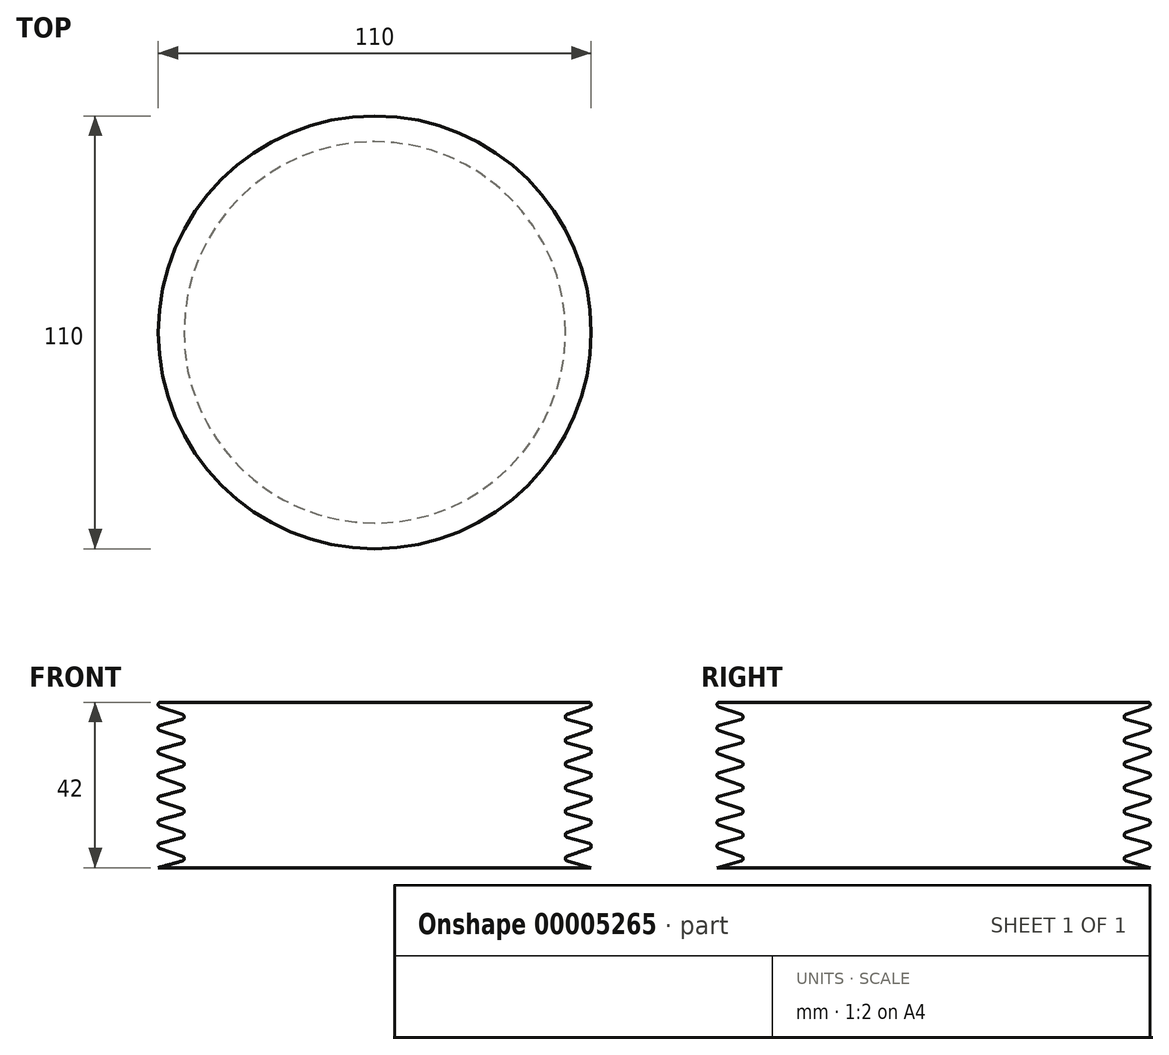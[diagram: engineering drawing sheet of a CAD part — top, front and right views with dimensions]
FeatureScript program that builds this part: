
annotation { "Feature Type Name" : "Feature", "Feature Type Description" : "" }
export const myFeature = defineFeature(function(context is Context, id is Id, definition is map)
    precondition{}
    {
        {
            var Q0;
            Q0=qCreatedBy(makeId("Front.planeOp"),FACE);
            var sketch = newSketch(context, id + "F0", { "sketchPlane" : qUnion([Q0])});
            skLineSegment(sketch, "E0", {"start": v(0, 0) * mm, "end": v(0, 42) * mm});
            skLineSegment(sketch, "E1", {"start": v(-55, 0) * mm, "end": v(-48.46, 1.8) * mm});
            skLineSegment(sketch, "E2", {"start": v(-48.46, 1.8) * mm, "end": v(-48.46, 2.8) * mm});
            skLineSegment(sketch, "E3", {"start": v(-48.46, 2.8) * mm, "end": v(-55, 5) * mm});
            skLineSegment(sketch, "E4", {"start": v(-55, 5) * mm, "end": v(-55, 6) * mm});
            skLineSegment(sketch, "E5.0.1.0", {"start": v(-55, 6) * mm, "end": v(-48.46, 7.8) * mm});
            skLineSegment(sketch, "E5.0.1.1", {"start": v(-48.46, 8.8) * mm, "end": v(-55, 11) * mm});
            skLineSegment(sketch, "E5.0.1.2", {"start": v(-55, 11) * mm, "end": v(-55, 12) * mm});
            skLineSegment(sketch, "E5.0.1.3", {"start": v(-48.46, 7.8) * mm, "end": v(-48.46, 8.8) * mm});
            skLineSegment(sketch, "E5.0.2.0", {"start": v(-55, 12) * mm, "end": v(-48.46, 13.8) * mm});
            skLineSegment(sketch, "E5.0.2.1", {"start": v(-48.46, 14.8) * mm, "end": v(-55, 17) * mm});
            skLineSegment(sketch, "E5.0.2.2", {"start": v(-55, 17) * mm, "end": v(-55, 18) * mm});
            skLineSegment(sketch, "E5.0.2.3", {"start": v(-48.46, 13.8) * mm, "end": v(-48.46, 14.8) * mm});
            skLineSegment(sketch, "E5.0.3.0", {"start": v(-55, 18) * mm, "end": v(-48.46, 19.8) * mm});
            skLineSegment(sketch, "E5.0.3.1", {"start": v(-48.46, 20.8) * mm, "end": v(-55, 23) * mm});
            skLineSegment(sketch, "E5.0.3.2", {"start": v(-55, 23) * mm, "end": v(-55, 24) * mm});
            skLineSegment(sketch, "E5.0.3.3", {"start": v(-48.46, 19.8) * mm, "end": v(-48.46, 20.8) * mm});
            skLineSegment(sketch, "E5.0.4.0", {"start": v(-55, 24) * mm, "end": v(-48.46, 25.8) * mm});
            skLineSegment(sketch, "E5.0.4.1", {"start": v(-48.46, 26.8) * mm, "end": v(-55, 29) * mm});
            skLineSegment(sketch, "E5.0.4.2", {"start": v(-55, 29) * mm, "end": v(-55, 30) * mm});
            skLineSegment(sketch, "E5.0.4.3", {"start": v(-48.46, 25.8) * mm, "end": v(-48.46, 26.8) * mm});
            skLineSegment(sketch, "E5.0.5.0", {"start": v(-55, 30) * mm, "end": v(-48.46, 31.8) * mm});
            skLineSegment(sketch, "E5.0.5.1", {"start": v(-48.46, 32.8) * mm, "end": v(-55, 35) * mm});
            skLineSegment(sketch, "E5.0.5.2", {"start": v(-55, 35) * mm, "end": v(-55, 36) * mm});
            skLineSegment(sketch, "E5.0.5.3", {"start": v(-48.46, 31.8) * mm, "end": v(-48.46, 32.8) * mm});
            skLineSegment(sketch, "E5.0.6.0", {"start": v(-55, 36) * mm, "end": v(-48.46, 37.8) * mm});
            skLineSegment(sketch, "E5.0.6.1", {"start": v(-48.46, 38.8) * mm, "end": v(-55, 41) * mm});
            skLineSegment(sketch, "E5.0.6.2", {"start": v(-55, 41) * mm, "end": v(-55, 42) * mm});
            skLineSegment(sketch, "E5.0.6.3", {"start": v(-48.46, 37.8) * mm, "end": v(-48.46, 38.8) * mm});
            skLineSegment(sketch, "E5.direction1", {"start": v(-55, 0) * mm, "end": v(-14, 0) * mm, "construction": true});
            skLineSegment(sketch, "E5.direction2", {"start": v(-55, 0) * mm, "end": v(-55, 6) * mm, "construction": true});
            skLineSegment(sketch, "E6", {"start": v(-55, 0) * mm, "end": v(0, 0) * mm});
            skLineSegment(sketch, "E7", {"start": v(-55, 42) * mm, "end": v(0, 42) * mm});
            skSolve(sketch);
        }
        {
            var Q0;
            Q0=makeQuery(id+"F0.imprint","IMPRINT",FACE,{"disambiguationData":[TD([[makeQuery(id+"F0.imprint","IMPRINT",EDGE,{"derivedFrom":sQuery(id+"F0.wireOp",EDGE,"E0")}),1.0]])]});
            var Q1;
            Q1=sQuery(id+"F0.wireOp",EDGE,"E0");
            revolve(context, id + "F1", {"entities" : qUnion([Q0]), "axis" : qUnion([Q1]), "revolveType" : RevolveType.FULL});
        }
        {
            var Q0;
            Q0=makeQuery(id+"F1.opRevolve","SWEPT_EDGE",EDGE,{"disambiguationData":[OSD([sQuery(id+"F0.wireOp",EDGE,"E5.0.6.1"),sQuery(id+"F0.wireOp",EDGE,"E5.0.6.2")])]});
            var Q1;
            Q1=makeQuery(id+"F1.opRevolve","SWEPT_EDGE",EDGE,{"disambiguationData":[OSD([sQuery(id+"F0.wireOp",EDGE,"E5.0.6.2"),sQuery(id+"F0.wireOp",EDGE,"E7")])]});
            var Q2;
            Q2=makeQuery(id+"F1.opRevolve","SWEPT_EDGE",EDGE,{"disambiguationData":[OSD([sQuery(id+"F0.wireOp",EDGE,"E5.0.6.1"),sQuery(id+"F0.wireOp",EDGE,"E5.0.6.3")])]});
            var Q3;
            Q3=makeQuery(id+"F1.opRevolve","SWEPT_EDGE",EDGE,{"disambiguationData":[OSD([sQuery(id+"F0.wireOp",EDGE,"E5.0.6.0"),sQuery(id+"F0.wireOp",EDGE,"E5.0.6.3")])]});
            var Q4;
            Q4=makeQuery(id+"F1.opRevolve","SWEPT_EDGE",EDGE,{"disambiguationData":[OSD([sQuery(id+"F0.wireOp",EDGE,"E5.0.5.2"),sQuery(id+"F0.wireOp",EDGE,"E5.0.6.0")])]});
            var Q5;
            Q5=makeQuery(id+"F1.opRevolve","SWEPT_FACE",FACE,{"disambiguationData":[OSD([sQuery(id+"F0.wireOp",EDGE,"E5.0.5.2")])]});
            var Q6;
            Q6=makeQuery(id+"F1.opRevolve","SWEPT_EDGE",EDGE,{"disambiguationData":[OSD([sQuery(id+"F0.wireOp",EDGE,"E5.0.5.1"),sQuery(id+"F0.wireOp",EDGE,"E5.0.5.2")])]});
            var Q7;
            Q7=makeQuery(id+"F1.opRevolve","SWEPT_EDGE",EDGE,{"disambiguationData":[OSD([sQuery(id+"F0.wireOp",EDGE,"E5.0.4.2"),sQuery(id+"F0.wireOp",EDGE,"E5.0.5.0")])]});
            var Q8;
            Q8=makeQuery(id+"F1.opRevolve","SWEPT_EDGE",EDGE,{"disambiguationData":[OSD([sQuery(id+"F0.wireOp",EDGE,"E5.0.4.1"),sQuery(id+"F0.wireOp",EDGE,"E5.0.4.2")])]});
            var Q9;
            Q9=makeQuery(id+"F1.opRevolve","SWEPT_EDGE",EDGE,{"disambiguationData":[OSD([sQuery(id+"F0.wireOp",EDGE,"E5.0.3.2"),sQuery(id+"F0.wireOp",EDGE,"E5.0.4.0")])]});
            var Q10;
            Q10=makeQuery(id+"F1.opRevolve","SWEPT_EDGE",EDGE,{"disambiguationData":[OSD([sQuery(id+"F0.wireOp",EDGE,"E5.0.3.1"),sQuery(id+"F0.wireOp",EDGE,"E5.0.3.2")])]});
            var Q11;
            Q11=makeQuery(id+"F1.opRevolve","SWEPT_EDGE",EDGE,{"disambiguationData":[OSD([sQuery(id+"F0.wireOp",EDGE,"E5.0.3.0"),sQuery(id+"F0.wireOp",EDGE,"E5.0.3.3")])]});
            var Q12;
            Q12=makeQuery(id+"F1.opRevolve","SWEPT_EDGE",EDGE,{"disambiguationData":[OSD([sQuery(id+"F0.wireOp",EDGE,"E5.0.3.1"),sQuery(id+"F0.wireOp",EDGE,"E5.0.3.3")])]});
            var Q13;
            Q13=makeQuery(id+"F1.opRevolve","SWEPT_EDGE",EDGE,{"disambiguationData":[OSD([sQuery(id+"F0.wireOp",EDGE,"E5.0.4.0"),sQuery(id+"F0.wireOp",EDGE,"E5.0.4.3")])]});
            var Q14;
            Q14=makeQuery(id+"F1.opRevolve","SWEPT_EDGE",EDGE,{"disambiguationData":[OSD([sQuery(id+"F0.wireOp",EDGE,"E5.0.4.1"),sQuery(id+"F0.wireOp",EDGE,"E5.0.4.3")])]});
            var Q15;
            Q15=makeQuery(id+"F1.opRevolve","SWEPT_EDGE",EDGE,{"disambiguationData":[OSD([sQuery(id+"F0.wireOp",EDGE,"E5.0.5.0"),sQuery(id+"F0.wireOp",EDGE,"E5.0.5.3")])]});
            var Q16;
            Q16=makeQuery(id+"F1.opRevolve","SWEPT_EDGE",EDGE,{"disambiguationData":[OSD([sQuery(id+"F0.wireOp",EDGE,"E5.0.5.1"),sQuery(id+"F0.wireOp",EDGE,"E5.0.5.3")])]});
            var Q17;
            Q17=makeQuery(id+"F1.opRevolve","SWEPT_EDGE",EDGE,{"disambiguationData":[OSD([sQuery(id+"F0.wireOp",EDGE,"E5.0.2.2"),sQuery(id+"F0.wireOp",EDGE,"E5.0.3.0")])]});
            var Q18;
            Q18=makeQuery(id+"F1.opRevolve","SWEPT_EDGE",EDGE,{"disambiguationData":[OSD([sQuery(id+"F0.wireOp",EDGE,"E5.0.2.1"),sQuery(id+"F0.wireOp",EDGE,"E5.0.2.2")])]});
            var Q19;
            Q19=makeQuery(id+"F1.opRevolve","SWEPT_EDGE",EDGE,{"disambiguationData":[OSD([sQuery(id+"F0.wireOp",EDGE,"E5.0.2.1"),sQuery(id+"F0.wireOp",EDGE,"E5.0.2.3")])]});
            var Q20;
            Q20=makeQuery(id+"F1.opRevolve","SWEPT_EDGE",EDGE,{"disambiguationData":[OSD([sQuery(id+"F0.wireOp",EDGE,"E5.0.2.0"),sQuery(id+"F0.wireOp",EDGE,"E5.0.2.3")])]});
            var Q21;
            Q21=makeQuery(id+"F1.opRevolve","SWEPT_FACE",FACE,{"disambiguationData":[OSD([sQuery(id+"F0.wireOp",EDGE,"E5.0.2.0")])]});
            var Q22;
            Q22=makeQuery(id+"F1.opRevolve","SWEPT_EDGE",EDGE,{"disambiguationData":[OSD([sQuery(id+"F0.wireOp",EDGE,"E5.0.1.2"),sQuery(id+"F0.wireOp",EDGE,"E5.0.2.0")])]});
            var Q23;
            Q23=makeQuery(id+"F1.opRevolve","SWEPT_EDGE",EDGE,{"disambiguationData":[OSD([sQuery(id+"F0.wireOp",EDGE,"E5.0.1.1"),sQuery(id+"F0.wireOp",EDGE,"E5.0.1.2")])]});
            var Q24;
            Q24=makeQuery(id+"F1.opRevolve","SWEPT_EDGE",EDGE,{"disambiguationData":[OSD([sQuery(id+"F0.wireOp",EDGE,"E5.0.1.0"),sQuery(id+"F0.wireOp",EDGE,"E5.0.1.3")])]});
            var Q25;
            Q25=makeQuery(id+"F1.opRevolve","SWEPT_EDGE",EDGE,{"disambiguationData":[OSD([sQuery(id+"F0.wireOp",EDGE,"E5.0.1.1"),sQuery(id+"F0.wireOp",EDGE,"E5.0.1.3")])]});
            var Q26;
            Q26=makeQuery(id+"F1.opRevolve","SWEPT_EDGE",EDGE,{"disambiguationData":[OSD([sQuery(id+"F0.wireOp",EDGE,"E4"),sQuery(id+"F0.wireOp",EDGE,"E5.0.1.0")])]});
            var Q27;
            Q27=makeQuery(id+"F1.opRevolve","SWEPT_EDGE",EDGE,{"disambiguationData":[OSD([sQuery(id+"F0.wireOp",EDGE,"E3"),sQuery(id+"F0.wireOp",EDGE,"E4")])]});
            var Q28;
            Q28=makeQuery(id+"F1.opRevolve","SWEPT_EDGE",EDGE,{"disambiguationData":[OSD([sQuery(id+"F0.wireOp",EDGE,"E2"),sQuery(id+"F0.wireOp",EDGE,"E3")])]});
            var Q29;
            Q29=makeQuery(id+"F1.opRevolve","SWEPT_EDGE",EDGE,{"disambiguationData":[OSD([sQuery(id+"F0.wireOp",EDGE,"E1"),sQuery(id+"F0.wireOp",EDGE,"E2")])]});
            fillet(context, id + "F2", {"entities" : qUnion([Q0, Q1, Q2, Q3, Q4, Q5, Q6, Q7, Q8, Q9, Q10, Q11, Q12, Q13, Q14, Q15, Q16, Q17, Q18, Q19, Q20, Q21, Q22, Q23, Q24, Q25, Q26, Q27, Q28, Q29]), "radius" : 0.55 * mm, "tangentPropagation" : true, "allowEdgeOverflow" : false});
        }
    });
